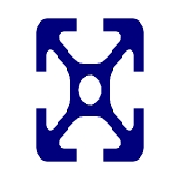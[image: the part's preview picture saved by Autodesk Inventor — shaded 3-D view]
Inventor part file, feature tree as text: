
AUTODESK INVENTOR PART (.ipt)
format: ipt  version: 2020 (Build 240168000, 168)  size: 273,408 bytes
history: native  units: mm
features: other x16, sketch x8, plane x1, split x1
ambient origin geometry x8: Origin, YZ Plane, XZ Plane, XY Plane, X Axis, Y Axis, Z Axis, Center Point
bodies: Body (feature_tree)
feature tree (26):
  other  "Řízená délka"
  other  "Těleso1"
  other  "Start Plane"
  other  "End Plane"
  other  "iFeatureSketch"
  other  "DRAZKA_20:1"
  other  "DRAZKA_20:2"
  other  "DRAZKA_20:3"
  other  "DRAZKA_20:4"
  other  "DIRA_20:1"
  other  "DRAZKA_20:1Axis"
  other  "DRAZKA_20:2Axis"
  other  "DRAZKA_20:3Axis"
  other  "DRAZKA_20:4Axis"
  other  "DIRA_20:1Axis"
  plane  "Work Plane5"
  split  "Split1"
  sketch  "Sketch"  dims[d2=20.0mm d3=20.0mm d4=2.0mm d9=-0.0mm d10=410.0mm d11=0.13mm d12=0.0mm d15=0.83mm d16=0.83mm d17=9.8mm d18=3.0mm d19=4.55mm d20=45.0deg d21=5.2mm d22=1.8mm d24=1.0mm d26=0.83mm d27=0.83mm d28=9.8mm d29=3.0mm d30=4.55mm d31=45.0deg d32=5.2mm d33=1.8mm d35=1.0mm d37=0.83mm d38=0.83mm d39=9.8mm d40=3.0mm d41=4.55mm d42=45.0deg d43=5.2mm d44=1.8mm d46=1.0mm d48=0.83mm d49=0.83mm d50=9.8mm d51=3.0mm d52=4.55mm d53=45.0deg d54=5.2mm d55=1.8mm d57=1.0mm d59=4.3mm d60=0.0mm d61=0.0mm d62=0.0mm d63=0.0mm d64=0.0mm d65=0.0mm d66=0.0mm d67=0.0mm d76=90.0deg d14=410.0mm]
  sketch  "Náčrt11"
  other  "Pracovní rovina4"
  sketch  "Náčrt12"
  sketch  "Náčrt6"
  sketch  "Náčrt7"
  sketch  "Náčrt8"
  sketch  "Náčrt9"
  sketch  "Náčrt10"
